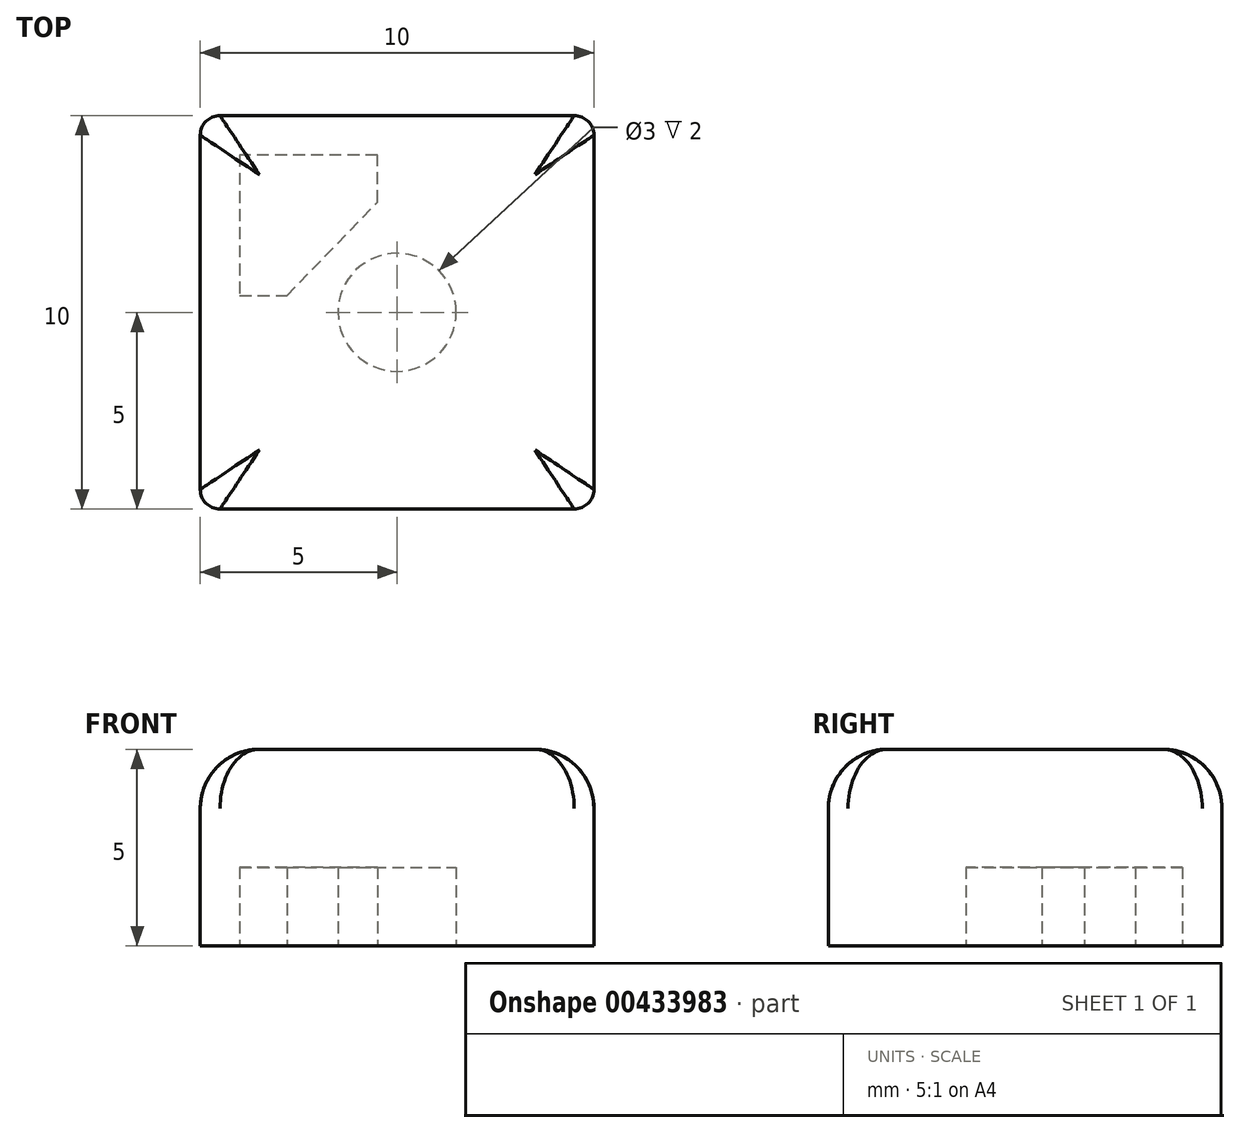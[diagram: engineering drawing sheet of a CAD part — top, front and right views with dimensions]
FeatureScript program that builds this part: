
annotation { "Feature Type Name" : "Feature", "Feature Type Description" : "" }
export const myFeature = defineFeature(function(context is Context, id is Id, definition is map)
    precondition{}
    {
        {
            var Q0;
            Q0=qCreatedBy(makeId("Top.planeOp"),FACE);
            var sketch = newSketch(context, id + "F0", { "sketchPlane" : qUnion([Q0])});
            skLineSegment(sketch, "E0.bottom", {"start": v(5, -5) * mm, "end": v(-5, -5) * mm});
            skLineSegment(sketch, "E0.top", {"start": v(5, 5) * mm, "end": v(-5, 5) * mm});
            skLineSegment(sketch, "E0.left", {"start": v(5, -5) * mm, "end": v(5, 5) * mm});
            skLineSegment(sketch, "E0.right", {"start": v(-5, -5) * mm, "end": v(-5, 5) * mm});
            skPoint(sketch, "E0.middle", {"position": v(0, 0) * mm});
            skSolve(sketch);
        }
        {
            var Q0;
            Q0=makeQuery(id+"F0.imprint","IMPRINT",FACE,{"disambiguationData":[TD([[makeQuery(id+"F0.imprint","IMPRINT",EDGE,{"derivedFrom":sQuery(id+"F0.wireOp",EDGE,"E0.bottom")}),-1.0]])]});
            extrude(context, id + "F1", {"entities" : qUnion([Q0]), "depth" : 5 * mm});
        }
        {
            var Q0;
            Q0=makeQuery(id+"F1.opExtrude","CAP_EDGE",EDGE,{"disambiguationData":[OSD([sQuery(id+"F0.wireOp",EDGE,"E0.right")])],"isStart":false});
            var Q1;
            Q1=makeQuery(id+"F1.opExtrude","CAP_EDGE",EDGE,{"disambiguationData":[OSD([sQuery(id+"F0.wireOp",EDGE,"E0.bottom")])],"isStart":false});
            var Q2;
            Q2=makeQuery(id+"F1.opExtrude","CAP_EDGE",EDGE,{"disambiguationData":[OSD([sQuery(id+"F0.wireOp",EDGE,"E0.left")])],"isStart":false});
            var Q3;
            Q3=makeQuery(id+"F1.opExtrude","CAP_EDGE",EDGE,{"disambiguationData":[OSD([sQuery(id+"F0.wireOp",EDGE,"E0.top")])],"isStart":false});
            fillet(context, id + "F2", {"entities" : qUnion([Q0, Q1, Q2, Q3]), "radius" : 1.5 * mm, "tangentPropagation" : true, "allowEdgeOverflow" : false});
        }
        {
            var Q0;
            Q0=makeQuery(id+"F1.opExtrude","CAP_FACE",FACE,{"disambiguationData":[OSD([sQuery(id+"F0.wireOp",EDGE,"E0.bottom"),sQuery(id+"F0.wireOp",EDGE,"E0.top"),sQuery(id+"F0.wireOp",EDGE,"E0.left"),sQuery(id+"F0.wireOp",EDGE,"E0.right")])],"isStart":true});
            var sketch = newSketch(context, id + "F3", { "sketchPlane" : qUnion([Q0])});
            skCircle(sketch, "E1", {"center": v(0, 0) * mm, "radius": 1.5 * mm});
            skSolve(sketch);
        }
        {
            var Q0;
            Q0=makeQuery(id+"F3.imprint","IMPRINT",FACE,{"disambiguationData":[TD([[makeQuery(id+"F3.imprint","IMPRINT",EDGE,{"derivedFrom":sQuery(id+"F3.wireOp",EDGE,"E1")}),1.0]])]});
            extrude(context, id + "F4", {"entities" : qUnion([Q0]), "operationType" : NewBodyOperationType.REMOVE, "oppositeDirection" : true, "depth" : 2 * mm});
        }
        {
            var Q0;
            Q0=makeQuery(id+"F1.opExtrude","CAP_FACE",FACE,{"disambiguationData":[OSD([sQuery(id+"F0.wireOp",EDGE,"E0.bottom"),sQuery(id+"F0.wireOp",EDGE,"E0.top"),sQuery(id+"F0.wireOp",EDGE,"E0.left"),sQuery(id+"F0.wireOp",EDGE,"E0.right")])],"isStart":true});
            var sketch = newSketch(context, id + "F5", { "sketchPlane" : qUnion([Q0])});
            skLineSegment(sketch, "E2", {"start": v(-0.5, -4) * mm, "end": v(-4, -4) * mm});
            skLineSegment(sketch, "E3", {"start": v(-4, -4) * mm, "end": v(-4, -0.43) * mm});
            skLineSegment(sketch, "E4", {"start": v(-4, -0.43) * mm, "end": v(-2.8, -0.43) * mm});
            skLineSegment(sketch, "E5", {"start": v(-2.8, -0.43) * mm, "end": v(-0.5, -2.8) * mm});
            skLineSegment(sketch, "E6", {"start": v(-0.5, -2.8) * mm, "end": v(-0.5, -4) * mm});
            skSolve(sketch);
        }
        {
            var Q0;
            Q0=makeQuery(id+"F5.imprint","IMPRINT",FACE,{"disambiguationData":[TD([[makeQuery(id+"F5.imprint","IMPRINT",EDGE,{"derivedFrom":sQuery(id+"F5.wireOp",EDGE,"E2")}),-1.0]])]});
            extrude(context, id + "F6", {"entities" : qUnion([Q0]), "operationType" : NewBodyOperationType.REMOVE, "oppositeDirection" : true, "depth" : 2 * mm});
        }
        {
            var Q0;
            Q0=makeQuery(id+"F1.opExtrude","SWEPT_EDGE",EDGE,{"disambiguationData":[OSD([sQuery(id+"F0.wireOp",EDGE,"E0.bottom"),sQuery(id+"F0.wireOp",EDGE,"E0.right")])]});
            var Q1;
            Q1=makeQuery(id+"F1.opExtrude","SWEPT_EDGE",EDGE,{"disambiguationData":[OSD([sQuery(id+"F0.wireOp",EDGE,"E0.bottom"),sQuery(id+"F0.wireOp",EDGE,"E0.left")])]});
            var Q2;
            Q2=makeQuery(id+"F1.opExtrude","SWEPT_EDGE",EDGE,{"disambiguationData":[OSD([sQuery(id+"F0.wireOp",EDGE,"E0.top"),sQuery(id+"F0.wireOp",EDGE,"E0.right")])]});
            var Q3;
            Q3=makeQuery(id+"F1.opExtrude","SWEPT_EDGE",EDGE,{"disambiguationData":[OSD([sQuery(id+"F0.wireOp",EDGE,"E0.top"),sQuery(id+"F0.wireOp",EDGE,"E0.left")])]});
            fillet(context, id + "F7", {"entities" : qUnion([Q0, Q1, Q2, Q3]), "radius" : 0.5 * mm, "tangentPropagation" : true, "allowEdgeOverflow" : false});
        }
    });
